# Revit family: S-tank_P
name_source: partatom
category: Оборудование
units: mm (PartAtom-declared; Revit-internal decimal feet)

## family parameters
Всегда вертикально = Да
Классификация = Нет
На основе рабочей плоскости = Нет
Общий = Нет
При загрузке вырезать с полостями = Нет
Размер круглого соединителя = Использовать диаметр
Тип детали = Нормальный
Точка расчета площади = Нет

## types (9) — shared parameters
ADSK_URL документации изделия = http://s-tank.ru
ADSK_Группирование = Оборудование
ADSK_Единица измерения = шт.
ADSK_Завод-изготовитель = ООО “С-ТЭНК ВОТЕР ХИТЕРС”
ADSK_Наименование = Бойлер косвенного нагрева
DN1 = 25 мм
DN2 = 15 мм
N = 1740 мм
shrf = 18 мм
Разработка семейств = https://rubim.tech

## per-type parameters (varying)
| type | A | ADSK_Код изделия | ADSK_Марка | ADSK_Масса | B | C | D | E | H | L | M | a | Диаметрcизоляцией |
| P150 | 198 мм | 4.0001 | P 150 | 51 | 308 мм | 438 мм | 548 мм | 618 мм | 925 мм | 198 мм | 745 мм | 96 мм | 575 мм |
| P200 | 208 мм | 4.0002 | P 200 | 58 | 328 мм | 508 мм | 688 мм | 758 мм | 1200 мм | 208 мм | 1020 мм | 96 мм | 575 мм |
| P300 | 198 мм | 4.0003 | P 300 | 70 | 318 мм | 538 мм | 658 мм | 728 мм | 1550 мм | 198 мм | 1360 мм | 96 мм | 575 мм |
| P400 | 259 мм | 4.0004 | P 400 | 85 | 389 мм | 619 мм | 749 мм | 819 мм | 1420 мм | 259 мм | 1110 мм | 121 мм | 725 мм |
| P500 | 259 мм | 4.0005 | P 500 | 93 | 389 мм | 619 мм | 749 мм | 819 мм | 1670 мм | 259 мм | 1360 мм | 121 мм | 725 мм |
| P750 | 301 мм | 4.0006 | P 750 | 114 | 431 мм | 621 мм | 751 мм | 831 мм | 1630 мм | 301 мм | 1326 мм | 153 мм | 920 мм |
| P1000 | 291 мм | 4.0007 | P 1000 | 145 | 481 мм | 701 мм | 891 мм | 1011 мм | 1630 мм | 291 мм | 1326 мм | 153 мм | 920 мм |
| P1500 | 295 мм | 4.0008 | P 1500 | 211 | 475 мм | 760 мм | 950 мм | 1075 мм | 2370 мм | 295 мм | 2010 мм | 178 мм | 1070 мм |
| P2000 | 323 мм | 4.0009 | P 2000 | 257 | 523 мм | 773 мм | 973 мм | 1093 мм | 2500 мм | 323 мм | 2178 мм | 197 мм | 1180 мм |

note: column(s) folded — value = type name in every type: ADSK_Обозначение
